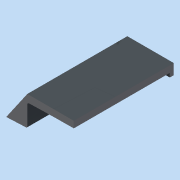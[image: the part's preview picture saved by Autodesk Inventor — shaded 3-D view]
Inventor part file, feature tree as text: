
AUTODESK INVENTOR PART (.ipt)
format: ipt  version: 2015 (Build 190159000, 159)  size: 670,720 bytes
history: native  units: in
note: dims shown in document units (in); Inventor stores cm internally (conversion verified against a paired STEP export)
features: split x5, other x3, plane x3
ambient origin geometry x8: Origin, YZ Plane, XZ Plane, XY Plane, X Axis, Y Axis, Z Axis, Center Point
bodies: Solid1 (feature_tree), Solid2 (feature_tree), Solid3 (feature_tree), Solid12 (feature_tree), Solid13 (feature_tree), Solid14 (feature_tree), Solid15 (feature_tree), Solid16 (feature_tree), Solid17 (feature_tree), Solid18 (feature_tree), Solid19 (feature_tree)
feature tree (11):
  other  "BatteryEnclosure.ipt"
  plane  "Work Plane1"
  plane  "Work Plane3"
  split  "Split1"
  split  "Split2"
  split  "Split3"
  split  "Split4"
  split  "Split5"
  other  "Solid2::BatteryEnclosure.ipt"
  other  "TaggingFeature1"
  plane  "Work Plane2"
